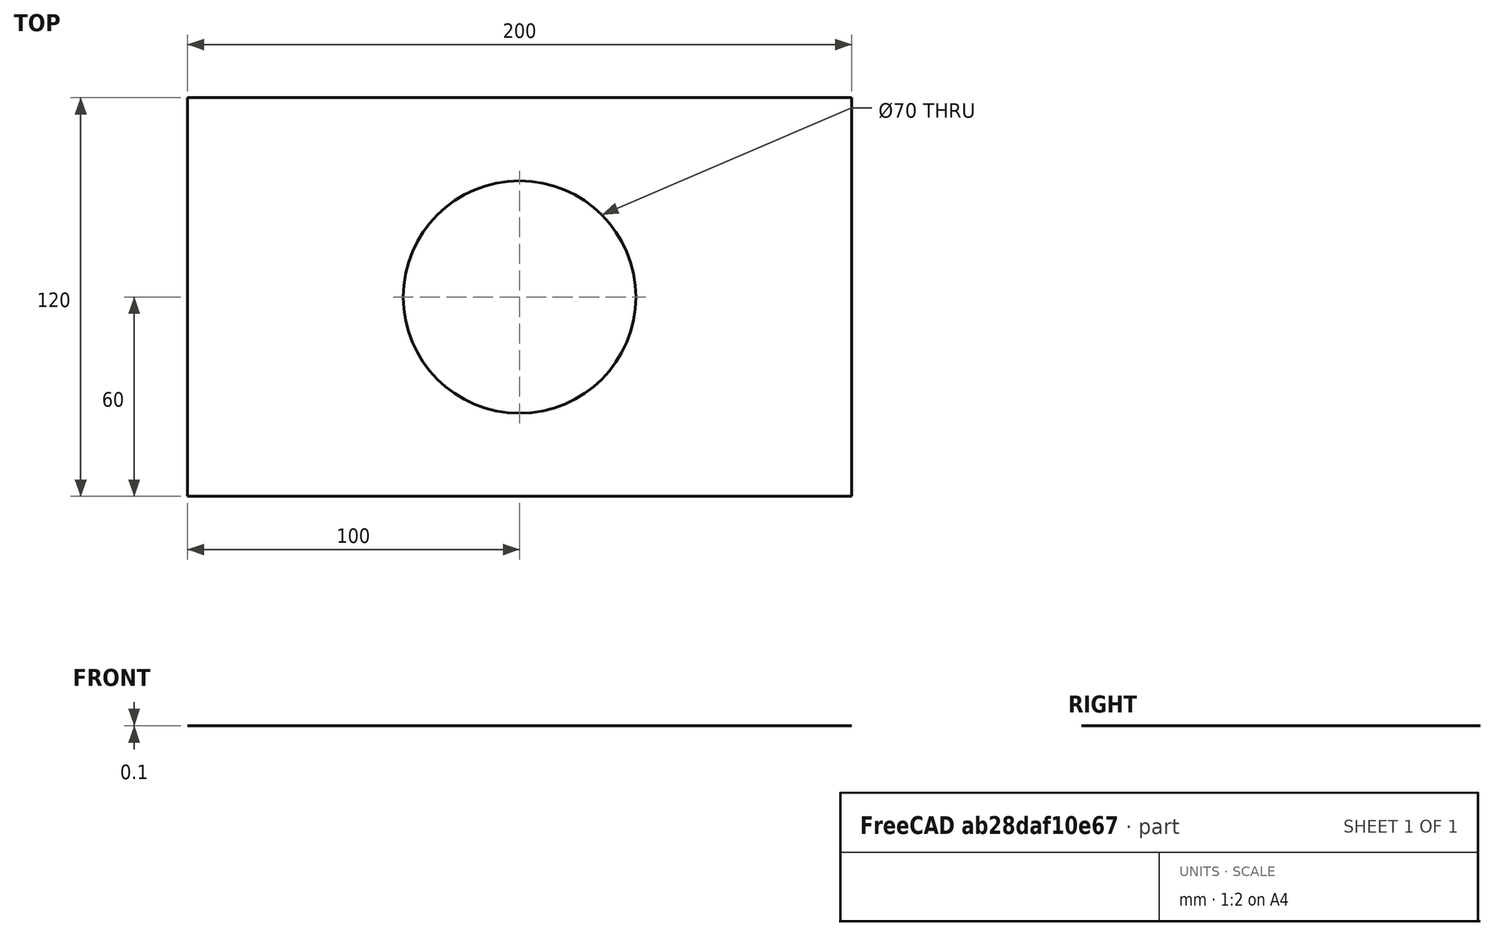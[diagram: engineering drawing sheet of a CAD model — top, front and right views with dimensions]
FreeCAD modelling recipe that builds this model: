
FCSTD DOCUMENT  (FreeCAD 0.19R24276 (Git))
Label: Master_sketch_120x200_P13
License: All rights reserved
LicenseURL: http://en.wikipedia.org/wiki/All_rights_reserved
objects: Sketcher::SketchObject×1, PartDesign::Pad×1, PartDesign::Body×1
note: 4 computed .brp shape members not serialized (recipe doc carries the construction recipe); baked Part::Feature solids carry a one-line shape summary decoded from their .brp

FEATURE [Sketcher::SketchObject] Sketch
  FullyConstrained = true
  MapMode = 5
  Support = -> [XY_Plane]
  sketch-geometry (5):
    g0: LineSegment StartX=-100 StartY=60 StartZ=0 EndX=100 EndY=60 EndZ=0
    g1: LineSegment StartX=100 StartY=60 StartZ=0 EndX=100 EndY=-60 EndZ=0
    g2: LineSegment StartX=100 StartY=-60 StartZ=0 EndX=-100 EndY=-60 EndZ=0
    g3: LineSegment StartX=-100 StartY=-60 StartZ=0 EndX=-100 EndY=60 EndZ=0
    g4: Circle CenterX=0 CenterY=0 CenterZ=0 NormalX=0 NormalY=0 NormalZ=1 AngleXU=0 Radius=35
  constraints (13):
    c: Coincident(g0,g1)
    c: Coincident(g1,g2)
    c: Coincident(g2,g3)
    c: Coincident(g3,g0)
    c: Horizontal(g0)
    c: Horizontal(g2)
    c: Vertical(g1)
    c: Vertical(g3)
    c: Symmetric(g0,g1,g-1)
    c: Coincident(g4,g-1)
    c: Diameter(g4) = 70
    c: DistanceX(g2,g2) = 200
    c: DistanceY(g1,g1) = 120
FEATURE [PartDesign::Pad] Pad
  Direction = (1,1,1)
  Length = 0.1
  Length2 = 100
  Profile = -> Sketch
  Type = 0
FEATURE [PartDesign::Body] Body
  Group = -> [Sketch,Pad]
  Origin = -> Origin
  Tip = -> Pad
